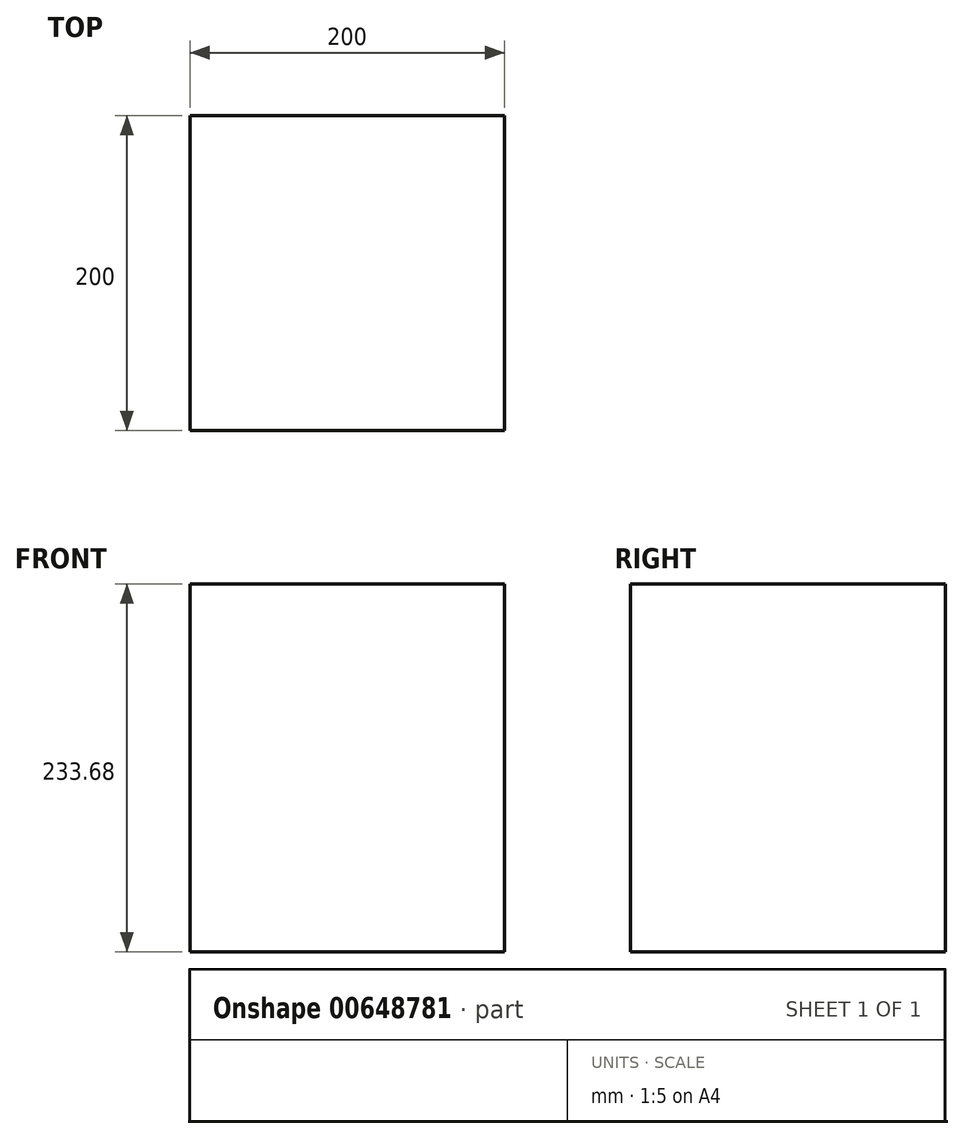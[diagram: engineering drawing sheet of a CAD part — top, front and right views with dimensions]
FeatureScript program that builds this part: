
annotation { "Feature Type Name" : "Feature", "Feature Type Description" : "" }
export const myFeature = defineFeature(function(context is Context, id is Id, definition is map)
    precondition{}
    {
        {
            var Q0;
            Q0=qCreatedBy(makeId("Top.planeOp"),FACE);
            var sketch = newSketch(context, id + "F0", { "sketchPlane" : qUnion([Q0])});
            skLineSegment(sketch, "E0.bottom", {"start": v(-100, 100) * mm, "end": v(100, 100) * mm});
            skLineSegment(sketch, "E0.top", {"start": v(-100, -100) * mm, "end": v(100, -100) * mm});
            skLineSegment(sketch, "E0.left", {"start": v(-100, 100) * mm, "end": v(-100, -100) * mm});
            skLineSegment(sketch, "E0.right", {"start": v(100, 100) * mm, "end": v(100, -100) * mm});
            skLineSegment(sketch, "E1", {"start": v(-100, 0) * mm, "end": v(0, 0) * mm, "construction": true});
            skLineSegment(sketch, "E2", {"start": v(0, 0) * mm, "end": v(0, 100) * mm, "construction": true});
            skSolve(sketch);
        }
        {
            var Q0;
            Q0=makeQuery(id+"F0.imprint","IMPRINT",FACE,{"disambiguationData":[TD([[makeQuery(id+"F0.imprint","IMPRINT",EDGE,{"derivedFrom":sQuery(id+"F0.wireOp",EDGE,"E0.bottom")}),-1.0]])]});
            extrude(context, id + "F1", {"entities" : qUnion([Q0]), "depth" : 233.68 * mm, "offsetDistance" : 25.4 * mm});
        }
    });
